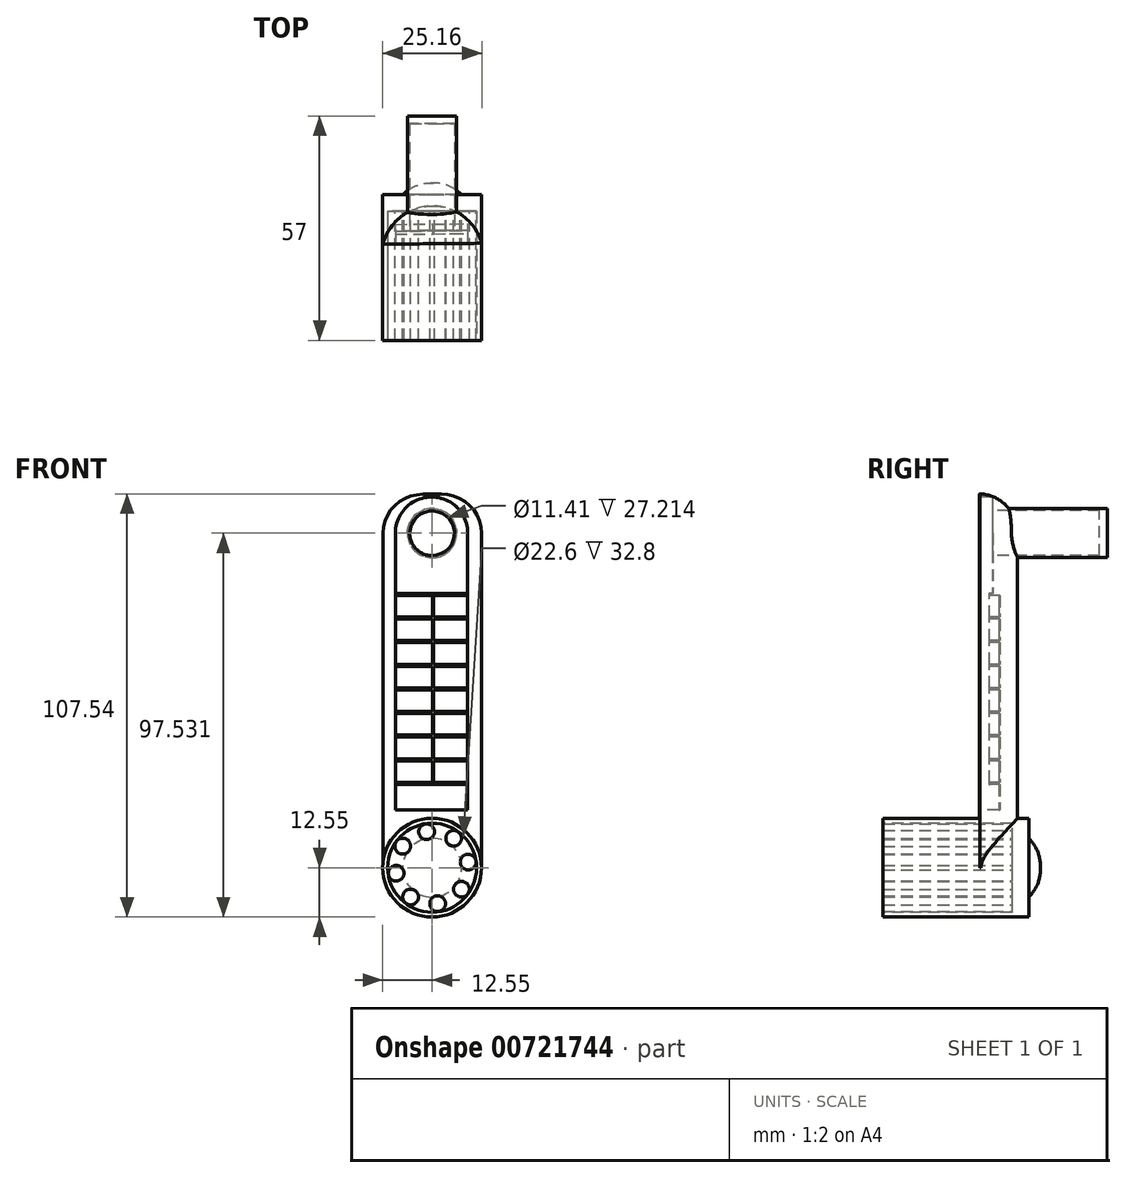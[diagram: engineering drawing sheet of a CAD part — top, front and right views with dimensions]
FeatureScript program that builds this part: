
annotation { "Feature Type Name" : "Feature", "Feature Type Description" : "" }
export const myFeature = defineFeature(function(context is Context, id is Id, definition is map)
    precondition{}
    {
        {
            var Q0;
            Q0=qCreatedBy(makeId("Front.planeOp"),FACE);
            var sketch = newSketch(context, id + "F0", { "sketchPlane" : qUnion([Q0])});
            skCircle(sketch, "E0", {"center": v(0, 0) * mm, "radius": 12.55 * mm});
            skSolve(sketch);
        }
        {
            var Q0;
            Q0=makeQuery(id+"F0.imprint","IMPRINT",FACE,{"disambiguationData":[TD([[makeQuery(id+"F0.imprint","IMPRINT",EDGE,{"derivedFrom":sQuery(id+"F0.wireOp",EDGE,"E0")}),1.0]])]});
            extrude(context, id + "F1", {"entities" : qUnion([Q0]), "depth" : 37 * mm, "offsetDistance" : 25 * mm});
        }
        {
            var Q0;
            Q0=qCreatedBy(makeId("Front.planeOp"),FACE);
            var sketch = newSketch(context, id + "F2", { "sketchPlane" : qUnion([Q0])});
            skCircle(sketch, "E1", {"center": v(0, 0) * mm, "radius": 7.5 * mm});
            skSolve(sketch);
        }
        {
            var Q0;
            Q0=qSketchRegion(id+"F2",true);
            extrude(context, id + "F3", {"entities" : qUnion([Q0]), "operationType" : NewBodyOperationType.ADD, "oppositeDirection" : true, "depth" : 3 * mm, "offsetDistance" : 25 * mm});
        }
        {
            var Q0;
            Q0=makeQuery(id+"F3.opExtrude","CAP_FACE",FACE,{"disambiguationData":[OSD([sQuery(id+"F2.wireOp",EDGE,"E1")])],"isStart":false});
            fillet(context, id + "F4", {"entities" : qUnion([Q0]), "radius" : 10 * mm, "tangentPropagation" : true, "allowEdgeOverflow" : false});
        }
        {
            var Q0;
            Q0=qCreatedBy(makeId("Top.planeOp"),FACE);
            var sketch = newSketch(context, id + "F5", { "sketchPlane" : qUnion([Q0])});
            skArc(sketch, "E2", {"start": v(12.6, -12.34) * mm, "mid": v(-0.03, -2.85) * mm, "end": v(-12.5, -12.58) * mm});
            skLineSegment(sketch, "E3", {"start": v(-12.5, -12.58) * mm, "end": v(12.6, -12.34) * mm});
            skSolve(sketch);
        }
        {
            var Q0;
            Q0=qSketchRegion(id+"F5",true);
            extrude(context, id + "F6", {"entities" : qUnion([Q0]), "operationType" : NewBodyOperationType.ADD, "depth" : 95 * mm, "offsetDistance" : 25 * mm});
        }
        {
            var Q0;
            Q0=makeQuery(id+"F6.opExtrude","CAP_EDGE",EDGE,{"disambiguationData":[OSD([sQuery(id+"F5.wireOp",EDGE,"E2")])],"isStart":false});
            fillet(context, id + "F7", {"entities" : qUnion([Q0]), "radius" : 10 * mm, "tangentPropagation" : true, "allowEdgeOverflow" : false});
        }
        {
            var Q0;
            Q0=qCreatedBy(makeId("Front.planeOp"),FACE);
            cPlane(context, id + "F8", {"entities" : qUnion([Q0]), "cplaneType" : CPlaneType.OFFSET, "offset" : 10 * mm, "width" : 150 * mm, "height" : 150 * mm});
        }
        {
            var Q0;
            Q0=qCreatedBy(id+"F8.planeOp",FACE);
            var sketch = newSketch(context, id + "F9", { "sketchPlane" : qUnion([Q0])});
            skCircle(sketch, "E4", {"center": v(-0.03, 85) * mm, "radius": 6.25 * mm});
            skSolve(sketch);
        }
        {
            var Q0;
            Q0=qSketchRegion(id+"F9",true);
            extrude(context, id + "F10", {"entities" : qUnion([Q0]), "operationType" : NewBodyOperationType.ADD, "oppositeDirection" : true, "depth" : 30 * mm, "offsetDistance" : 25 * mm});
        }
        {
            var Q0;
            Q0=makeQuery(id+"F6.opExtrude","SWEPT_FACE",FACE,{"disambiguationData":[OSD([sQuery(id+"F5.wireOp",EDGE,"E3")])]});
            var sketch = newSketch(context, id + "F11", { "sketchPlane" : qUnion([Q0])});
            skLineSegment(sketch, "E5.bottom", {"start": v(-9.45, 85) * mm, "end": v(8.93, 85) * mm});
            skLineSegment(sketch, "E5.top", {"start": v(-9.45, 14.71) * mm, "end": v(8.93, 14.71) * mm});
            skLineSegment(sketch, "E5.left", {"start": v(-9.45, 85) * mm, "end": v(-9.45, 14.71) * mm});
            skLineSegment(sketch, "E5.right", {"start": v(8.93, 85) * mm, "end": v(8.93, 14.71) * mm});
            skArc(sketch, "E6", {"start": v(8.93, 85) * mm, "mid": v(-0.26, 94.19) * mm, "end": v(-9.45, 85) * mm});
            skSolve(sketch);
        }
        {
            var Q0;
            Q0=makeQuery(id+"F11.imprint","IMPRINT",FACE,{"disambiguationData":[TD([[makeQuery(id+"F11.imprint","IMPRINT",EDGE,{"derivedFrom":sQuery(id+"F11.wireOp",EDGE,"E5.bottom")}),-1.0]])]});
            extrude(context, id + "F12", {"entities" : qUnion([Q0]), "operationType" : NewBodyOperationType.REMOVE, "oppositeDirection" : true, "depth" : 2 * mm, "offsetDistance" : 25 * mm});
        }
        {
            var Q0;
            Q0 = qSketchRegion(id + "F11", true);
            extrude(context, id + "F13", {"entities" : qUnion([Q0]), "operationType" : NewBodyOperationType.REMOVE, "oppositeDirection" : true, "depth" : 2.5 * mm, "offsetDistance" : 25 * mm});
        }
        {
            var Q0;
            Q0=makeQuery(id+"F13.boolean.opBoolean","COPY",FACE,{"derivedFrom":makeQuery(id+"F13.opExtrude","CAP_FACE",FACE,{"disambiguationData":[OSD([sQuery(id+"F11.wireOp",EDGE,"E5.top"),sQuery(id+"F11.wireOp",EDGE,"E5.left"),sQuery(id+"F11.wireOp",EDGE,"E5.right"),sQuery(id+"F11.wireOp",EDGE,"E6")])],"isStart":false})});
            var sketch = newSketch(context, id + "F14", { "sketchPlane" : qUnion([Q0])});
            skLineSegment(sketch, "E7", {"start": v(-9.45, 21.68) * mm, "end": v(8.93, 21.68) * mm});
            skLineSegment(sketch, "E8.0.1.0", {"start": v(-9.45, 27.68) * mm, "end": v(8.93, 27.68) * mm});
            skLineSegment(sketch, "E8.0.2.0", {"start": v(-9.45, 33.68) * mm, "end": v(8.93, 33.68) * mm});
            skLineSegment(sketch, "E8.0.3.0", {"start": v(-9.45, 39.68) * mm, "end": v(8.93, 39.68) * mm});
            skLineSegment(sketch, "E8.0.4.0", {"start": v(-9.45, 45.68) * mm, "end": v(8.93, 45.68) * mm});
            skLineSegment(sketch, "E8.0.5.0", {"start": v(-9.45, 51.68) * mm, "end": v(8.93, 51.68) * mm});
            skLineSegment(sketch, "E8.0.6.0", {"start": v(-9.45, 57.68) * mm, "end": v(8.93, 57.68) * mm});
            skLineSegment(sketch, "E8.0.7.0", {"start": v(-9.45, 63.68) * mm, "end": v(8.93, 63.68) * mm});
            skLineSegment(sketch, "E8.0.8.0", {"start": v(-9.45, 69.68) * mm, "end": v(8.93, 69.68) * mm});
            skLineSegment(sketch, "E8.direction1", {"start": v(-9.45, 21.68) * mm, "end": v(-9.45, 21.68) * mm});
            skLineSegment(sketch, "E8.direction2", {"start": v(-9.45, 21.68) * mm, "end": v(-9.45, 27.68) * mm, "construction": true});
            skLineSegment(sketch, "E9", {"start": v(0, 14.71) * mm, "end": v(0, 75.51) * mm});
            skLineSegment(sketch, "E10", {"start": v(-9.45, 21.16) * mm, "end": v(8.93, 21.16) * mm});
            skLineSegment(sketch, "E11.0.1.0", {"start": v(-9.45, 27.16) * mm, "end": v(8.93, 27.16) * mm});
            skLineSegment(sketch, "E11.0.2.0", {"start": v(-9.45, 33.16) * mm, "end": v(8.93, 33.16) * mm});
            skLineSegment(sketch, "E11.0.3.0", {"start": v(-9.45, 39.16) * mm, "end": v(8.93, 39.16) * mm});
            skLineSegment(sketch, "E11.0.4.0", {"start": v(-9.45, 45.16) * mm, "end": v(8.93, 45.16) * mm});
            skLineSegment(sketch, "E11.0.5.0", {"start": v(-9.45, 51.16) * mm, "end": v(8.93, 51.16) * mm});
            skLineSegment(sketch, "E11.0.6.0", {"start": v(-9.45, 57.16) * mm, "end": v(8.93, 57.16) * mm});
            skLineSegment(sketch, "E11.0.7.0", {"start": v(-9.45, 63.16) * mm, "end": v(8.93, 63.16) * mm});
            skLineSegment(sketch, "E11.0.8.0", {"start": v(-9.45, 69.16) * mm, "end": v(8.93, 69.16) * mm});
            skLineSegment(sketch, "E11.1.1.0", {"start": v(-9.45, 27.16) * mm, "end": v(8.93, 27.16) * mm});
            skLineSegment(sketch, "E11.1.2.0", {"start": v(-9.45, 33.16) * mm, "end": v(8.93, 33.16) * mm});
            skLineSegment(sketch, "E11.1.3.0", {"start": v(-9.45, 39.16) * mm, "end": v(8.93, 39.16) * mm});
            skLineSegment(sketch, "E11.1.4.0", {"start": v(-9.45, 45.16) * mm, "end": v(8.93, 45.16) * mm});
            skLineSegment(sketch, "E11.1.5.0", {"start": v(-9.45, 51.16) * mm, "end": v(8.93, 51.16) * mm});
            skLineSegment(sketch, "E11.1.6.0", {"start": v(-9.45, 57.16) * mm, "end": v(8.93, 57.16) * mm});
            skLineSegment(sketch, "E11.1.7.0", {"start": v(-9.45, 63.16) * mm, "end": v(8.93, 63.16) * mm});
            skLineSegment(sketch, "E11.1.8.0", {"start": v(-9.45, 69.16) * mm, "end": v(8.93, 69.16) * mm});
            skLineSegment(sketch, "E11.2.1.0", {"start": v(-9.45, 27.16) * mm, "end": v(8.93, 27.16) * mm});
            skLineSegment(sketch, "E11.2.2.0", {"start": v(-9.45, 33.16) * mm, "end": v(8.93, 33.16) * mm});
            skLineSegment(sketch, "E11.2.3.0", {"start": v(-9.45, 39.16) * mm, "end": v(8.93, 39.16) * mm});
            skLineSegment(sketch, "E11.2.4.0", {"start": v(-9.45, 45.16) * mm, "end": v(8.93, 45.16) * mm});
            skLineSegment(sketch, "E11.2.5.0", {"start": v(-9.45, 51.16) * mm, "end": v(8.93, 51.16) * mm});
            skLineSegment(sketch, "E11.2.6.0", {"start": v(-9.45, 57.16) * mm, "end": v(8.93, 57.16) * mm});
            skLineSegment(sketch, "E11.2.7.0", {"start": v(-9.45, 63.16) * mm, "end": v(8.93, 63.16) * mm});
            skLineSegment(sketch, "E11.2.8.0", {"start": v(-9.45, 69.16) * mm, "end": v(8.93, 69.16) * mm});
            skLineSegment(sketch, "E11.3.1.0", {"start": v(-9.45, 27.16) * mm, "end": v(8.93, 27.16) * mm});
            skLineSegment(sketch, "E11.3.2.0", {"start": v(-9.45, 33.16) * mm, "end": v(8.93, 33.16) * mm});
            skLineSegment(sketch, "E11.3.3.0", {"start": v(-9.45, 39.16) * mm, "end": v(8.93, 39.16) * mm});
            skLineSegment(sketch, "E11.3.4.0", {"start": v(-9.45, 45.16) * mm, "end": v(8.93, 45.16) * mm});
            skLineSegment(sketch, "E11.3.5.0", {"start": v(-9.45, 51.16) * mm, "end": v(8.93, 51.16) * mm});
            skLineSegment(sketch, "E11.3.6.0", {"start": v(-9.45, 57.16) * mm, "end": v(8.93, 57.16) * mm});
            skLineSegment(sketch, "E11.3.7.0", {"start": v(-9.45, 63.16) * mm, "end": v(8.93, 63.16) * mm});
            skLineSegment(sketch, "E11.3.8.0", {"start": v(-9.45, 69.16) * mm, "end": v(8.93, 69.16) * mm});
            skLineSegment(sketch, "E11.4.1.0", {"start": v(-9.45, 27.16) * mm, "end": v(8.93, 27.16) * mm});
            skLineSegment(sketch, "E11.4.2.0", {"start": v(-9.45, 33.16) * mm, "end": v(8.93, 33.16) * mm});
            skLineSegment(sketch, "E11.4.3.0", {"start": v(-9.45, 39.16) * mm, "end": v(8.93, 39.16) * mm});
            skLineSegment(sketch, "E11.4.4.0", {"start": v(-9.45, 45.16) * mm, "end": v(8.93, 45.16) * mm});
            skLineSegment(sketch, "E11.4.5.0", {"start": v(-9.45, 51.16) * mm, "end": v(8.93, 51.16) * mm});
            skLineSegment(sketch, "E11.4.6.0", {"start": v(-9.45, 57.16) * mm, "end": v(8.93, 57.16) * mm});
            skLineSegment(sketch, "E11.4.7.0", {"start": v(-9.45, 63.16) * mm, "end": v(8.93, 63.16) * mm});
            skLineSegment(sketch, "E11.4.8.0", {"start": v(-9.45, 69.16) * mm, "end": v(8.93, 69.16) * mm});
            skLineSegment(sketch, "E11.5.1.0", {"start": v(-9.45, 27.16) * mm, "end": v(8.93, 27.16) * mm});
            skLineSegment(sketch, "E11.5.2.0", {"start": v(-9.45, 33.16) * mm, "end": v(8.93, 33.16) * mm});
            skLineSegment(sketch, "E11.5.3.0", {"start": v(-9.45, 39.16) * mm, "end": v(8.93, 39.16) * mm});
            skLineSegment(sketch, "E11.5.4.0", {"start": v(-9.45, 45.16) * mm, "end": v(8.93, 45.16) * mm});
            skLineSegment(sketch, "E11.5.5.0", {"start": v(-9.45, 51.16) * mm, "end": v(8.93, 51.16) * mm});
            skLineSegment(sketch, "E11.5.6.0", {"start": v(-9.45, 57.16) * mm, "end": v(8.93, 57.16) * mm});
            skLineSegment(sketch, "E11.5.7.0", {"start": v(-9.45, 63.16) * mm, "end": v(8.93, 63.16) * mm});
            skLineSegment(sketch, "E11.5.8.0", {"start": v(-9.45, 69.16) * mm, "end": v(8.93, 69.16) * mm});
            skLineSegment(sketch, "E11.6.1.0", {"start": v(-9.45, 27.16) * mm, "end": v(8.93, 27.16) * mm});
            skLineSegment(sketch, "E11.6.2.0", {"start": v(-9.45, 33.16) * mm, "end": v(8.93, 33.16) * mm});
            skLineSegment(sketch, "E11.6.3.0", {"start": v(-9.45, 39.16) * mm, "end": v(8.93, 39.16) * mm});
            skLineSegment(sketch, "E11.6.4.0", {"start": v(-9.45, 45.16) * mm, "end": v(8.93, 45.16) * mm});
            skLineSegment(sketch, "E11.6.5.0", {"start": v(-9.45, 51.16) * mm, "end": v(8.93, 51.16) * mm});
            skLineSegment(sketch, "E11.6.6.0", {"start": v(-9.45, 57.16) * mm, "end": v(8.93, 57.16) * mm});
            skLineSegment(sketch, "E11.6.7.0", {"start": v(-9.45, 63.16) * mm, "end": v(8.93, 63.16) * mm});
            skLineSegment(sketch, "E11.6.8.0", {"start": v(-9.45, 69.16) * mm, "end": v(8.93, 69.16) * mm});
            skLineSegment(sketch, "E11.7.1.0", {"start": v(-9.45, 27.16) * mm, "end": v(8.93, 27.16) * mm});
            skLineSegment(sketch, "E11.7.2.0", {"start": v(-9.45, 33.16) * mm, "end": v(8.93, 33.16) * mm});
            skLineSegment(sketch, "E11.7.3.0", {"start": v(-9.45, 39.16) * mm, "end": v(8.93, 39.16) * mm});
            skLineSegment(sketch, "E11.7.4.0", {"start": v(-9.45, 45.16) * mm, "end": v(8.93, 45.16) * mm});
            skLineSegment(sketch, "E11.7.5.0", {"start": v(-9.45, 51.16) * mm, "end": v(8.93, 51.16) * mm});
            skLineSegment(sketch, "E11.7.6.0", {"start": v(-9.45, 57.16) * mm, "end": v(8.93, 57.16) * mm});
            skLineSegment(sketch, "E11.7.7.0", {"start": v(-9.45, 63.16) * mm, "end": v(8.93, 63.16) * mm});
            skLineSegment(sketch, "E11.7.8.0", {"start": v(-9.45, 69.16) * mm, "end": v(8.93, 69.16) * mm});
            skLineSegment(sketch, "E11.8.1.0", {"start": v(-9.45, 27.16) * mm, "end": v(8.93, 27.16) * mm});
            skLineSegment(sketch, "E11.8.2.0", {"start": v(-9.45, 33.16) * mm, "end": v(8.93, 33.16) * mm});
            skLineSegment(sketch, "E11.8.3.0", {"start": v(-9.45, 39.16) * mm, "end": v(8.93, 39.16) * mm});
            skLineSegment(sketch, "E11.8.4.0", {"start": v(-9.45, 45.16) * mm, "end": v(8.93, 45.16) * mm});
            skLineSegment(sketch, "E11.8.5.0", {"start": v(-9.45, 51.16) * mm, "end": v(8.93, 51.16) * mm});
            skLineSegment(sketch, "E11.8.6.0", {"start": v(-9.45, 57.16) * mm, "end": v(8.93, 57.16) * mm});
            skLineSegment(sketch, "E11.8.7.0", {"start": v(-9.45, 63.16) * mm, "end": v(8.93, 63.16) * mm});
            skLineSegment(sketch, "E11.8.8.0", {"start": v(-9.45, 69.16) * mm, "end": v(8.93, 69.16) * mm});
            skLineSegment(sketch, "E11.direction1", {"start": v(-9.45, 21.16) * mm, "end": v(-9.45, 21.16) * mm});
            skLineSegment(sketch, "E11.direction2", {"start": v(-9.45, 21.16) * mm, "end": v(-9.45, 27.16) * mm, "construction": true});
            skLineSegment(sketch, "E12", {"start": v(0.32, 14.71) * mm, "end": v(0.32, 75.5) * mm});
            skSolve(sketch);
        }
        {
            var Q0;
            {var subQ0=sQuery(id+"F14.wireOp",EDGE,"E9");var subQ1=makeQuery(id+"F13.boolean.opBoolean","COPY",EDGE,{"derivedFrom":makeQuery(id+"F13.opExtrude","CAP_EDGE",EDGE,{"disambiguationData":[OSD([sQuery(id+"F11.wireOp",EDGE,"E5.top")])],"isStart":false})});var subQ2=makeQuery(id+"F14.imprint","INTERSECT",VERTEX,{"derivedFrom":[subQ1,subQ0]});Q0=makeQuery(id+"F14.imprint","IMPRINT",FACE,{"disambiguationData":[TD([[makeQuery(id+"F14.imprint","IMPRINT",EDGE,{"disambiguationData":[TD([[subQ2,-1.0]])],"derivedFrom":subQ0}),1.0]])]});}
            var Q1;
            {var subQ0=sQuery(id+"F14.wireOp",EDGE,"E7");var subQ1=makeQuery(id+"F13.boolean.opBoolean","COPY",EDGE,{"derivedFrom":makeQuery(id+"F13.opExtrude","CAP_EDGE",EDGE,{"disambiguationData":[OSD([sQuery(id+"F11.wireOp",EDGE,"E5.left")])],"isStart":false})});var subQ2=makeQuery(id+"F14.imprint","INTERSECT",VERTEX,{"derivedFrom":[subQ1,subQ0]});Q1=makeQuery(id+"F14.imprint","IMPRINT",FACE,{"disambiguationData":[TD([[makeQuery(id+"F14.imprint","IMPRINT",EDGE,{"disambiguationData":[TD([[subQ2,-1.0]])],"derivedFrom":subQ0}),1.0]])]});}
            var Q2;
            {var subQ0=sQuery(id+"F14.wireOp",EDGE,"E8.0.1.0");var subQ1=makeQuery(id+"F13.boolean.opBoolean","COPY",EDGE,{"derivedFrom":makeQuery(id+"F13.opExtrude","CAP_EDGE",EDGE,{"disambiguationData":[OSD([sQuery(id+"F11.wireOp",EDGE,"E5.left")])],"isStart":false})});var subQ2=makeQuery(id+"F14.imprint","INTERSECT",VERTEX,{"derivedFrom":[subQ1,subQ0]});Q2=makeQuery(id+"F14.imprint","IMPRINT",FACE,{"disambiguationData":[TD([[makeQuery(id+"F14.imprint","IMPRINT",EDGE,{"disambiguationData":[TD([[subQ2,-1.0]])],"derivedFrom":subQ0}),1.0]])]});}
            var Q3;
            {var subQ0=sQuery(id+"F14.wireOp",EDGE,"E8.0.2.0");var subQ1=makeQuery(id+"F13.boolean.opBoolean","COPY",EDGE,{"derivedFrom":makeQuery(id+"F13.opExtrude","CAP_EDGE",EDGE,{"disambiguationData":[OSD([sQuery(id+"F11.wireOp",EDGE,"E5.left")])],"isStart":false})});var subQ2=makeQuery(id+"F14.imprint","INTERSECT",VERTEX,{"derivedFrom":[subQ1,subQ0]});Q3=makeQuery(id+"F14.imprint","IMPRINT",FACE,{"disambiguationData":[TD([[makeQuery(id+"F14.imprint","IMPRINT",EDGE,{"disambiguationData":[TD([[subQ2,-1.0]])],"derivedFrom":subQ0}),1.0]])]});}
            var Q4;
            {var subQ0=sQuery(id+"F14.wireOp",EDGE,"E8.0.3.0");var subQ1=makeQuery(id+"F13.boolean.opBoolean","COPY",EDGE,{"derivedFrom":makeQuery(id+"F13.opExtrude","CAP_EDGE",EDGE,{"disambiguationData":[OSD([sQuery(id+"F11.wireOp",EDGE,"E5.left")])],"isStart":false})});var subQ2=makeQuery(id+"F14.imprint","INTERSECT",VERTEX,{"derivedFrom":[subQ1,subQ0]});Q4=makeQuery(id+"F14.imprint","IMPRINT",FACE,{"disambiguationData":[TD([[makeQuery(id+"F14.imprint","IMPRINT",EDGE,{"disambiguationData":[TD([[subQ2,-1.0]])],"derivedFrom":subQ0}),1.0]])]});}
            var Q5;
            {var subQ0=sQuery(id+"F14.wireOp",EDGE,"E8.0.4.0");var subQ1=makeQuery(id+"F13.boolean.opBoolean","COPY",EDGE,{"derivedFrom":makeQuery(id+"F13.opExtrude","CAP_EDGE",EDGE,{"disambiguationData":[OSD([sQuery(id+"F11.wireOp",EDGE,"E5.left")])],"isStart":false})});var subQ2=makeQuery(id+"F14.imprint","INTERSECT",VERTEX,{"derivedFrom":[subQ1,subQ0]});Q5=makeQuery(id+"F14.imprint","IMPRINT",FACE,{"disambiguationData":[TD([[makeQuery(id+"F14.imprint","IMPRINT",EDGE,{"disambiguationData":[TD([[subQ2,-1.0]])],"derivedFrom":subQ0}),1.0]])]});}
            var Q6;
            {var subQ0=sQuery(id+"F14.wireOp",EDGE,"E8.0.5.0");var subQ1=makeQuery(id+"F13.boolean.opBoolean","COPY",EDGE,{"derivedFrom":makeQuery(id+"F13.opExtrude","CAP_EDGE",EDGE,{"disambiguationData":[OSD([sQuery(id+"F11.wireOp",EDGE,"E5.left")])],"isStart":false})});var subQ2=makeQuery(id+"F14.imprint","INTERSECT",VERTEX,{"derivedFrom":[subQ1,subQ0]});Q6=makeQuery(id+"F14.imprint","IMPRINT",FACE,{"disambiguationData":[TD([[makeQuery(id+"F14.imprint","IMPRINT",EDGE,{"disambiguationData":[TD([[subQ2,-1.0]])],"derivedFrom":subQ0}),1.0]])]});}
            var Q7;
            {var subQ0=sQuery(id+"F14.wireOp",EDGE,"E8.0.6.0");var subQ1=makeQuery(id+"F13.boolean.opBoolean","COPY",EDGE,{"derivedFrom":makeQuery(id+"F13.opExtrude","CAP_EDGE",EDGE,{"disambiguationData":[OSD([sQuery(id+"F11.wireOp",EDGE,"E5.left")])],"isStart":false})});var subQ2=makeQuery(id+"F14.imprint","INTERSECT",VERTEX,{"derivedFrom":[subQ1,subQ0]});Q7=makeQuery(id+"F14.imprint","IMPRINT",FACE,{"disambiguationData":[TD([[makeQuery(id+"F14.imprint","IMPRINT",EDGE,{"disambiguationData":[TD([[subQ2,-1.0]])],"derivedFrom":subQ0}),1.0]])]});}
            var Q8;
            {var subQ0=sQuery(id+"F14.wireOp",EDGE,"E8.0.7.0");var subQ1=makeQuery(id+"F13.boolean.opBoolean","COPY",EDGE,{"derivedFrom":makeQuery(id+"F13.opExtrude","CAP_EDGE",EDGE,{"disambiguationData":[OSD([sQuery(id+"F11.wireOp",EDGE,"E5.left")])],"isStart":false})});var subQ2=makeQuery(id+"F14.imprint","INTERSECT",VERTEX,{"derivedFrom":[subQ1,subQ0]});Q8=makeQuery(id+"F14.imprint","IMPRINT",FACE,{"disambiguationData":[TD([[makeQuery(id+"F14.imprint","IMPRINT",EDGE,{"disambiguationData":[TD([[subQ2,-1.0]])],"derivedFrom":subQ0}),1.0]])]});}
            var Q9;
            {var subQ0=sQuery(id+"F14.wireOp",EDGE,"E8.0.7.0");var subQ1=makeQuery(id+"F13.boolean.opBoolean","COPY",EDGE,{"derivedFrom":makeQuery(id+"F13.opExtrude","CAP_EDGE",EDGE,{"disambiguationData":[OSD([sQuery(id+"F11.wireOp",EDGE,"E5.right")])],"isStart":false})});var subQ2=makeQuery(id+"F14.imprint","INTERSECT",VERTEX,{"derivedFrom":[subQ1,subQ0]});Q9=makeQuery(id+"F14.imprint","IMPRINT",FACE,{"disambiguationData":[TD([[makeQuery(id+"F14.imprint","IMPRINT",EDGE,{"disambiguationData":[TD([[subQ2,1.0]])],"derivedFrom":subQ0}),1.0]])]});}
            var Q10;
            {var subQ0=sQuery(id+"F14.wireOp",EDGE,"E8.0.6.0");var subQ1=makeQuery(id+"F13.boolean.opBoolean","COPY",EDGE,{"derivedFrom":makeQuery(id+"F13.opExtrude","CAP_EDGE",EDGE,{"disambiguationData":[OSD([sQuery(id+"F11.wireOp",EDGE,"E5.right")])],"isStart":false})});var subQ2=makeQuery(id+"F14.imprint","INTERSECT",VERTEX,{"derivedFrom":[subQ1,subQ0]});Q10=makeQuery(id+"F14.imprint","IMPRINT",FACE,{"disambiguationData":[TD([[makeQuery(id+"F14.imprint","IMPRINT",EDGE,{"disambiguationData":[TD([[subQ2,1.0]])],"derivedFrom":subQ0}),1.0]])]});}
            var Q11;
            {var subQ0=sQuery(id+"F14.wireOp",EDGE,"E8.0.5.0");var subQ1=makeQuery(id+"F13.boolean.opBoolean","COPY",EDGE,{"derivedFrom":makeQuery(id+"F13.opExtrude","CAP_EDGE",EDGE,{"disambiguationData":[OSD([sQuery(id+"F11.wireOp",EDGE,"E5.right")])],"isStart":false})});var subQ2=makeQuery(id+"F14.imprint","INTERSECT",VERTEX,{"derivedFrom":[subQ1,subQ0]});Q11=makeQuery(id+"F14.imprint","IMPRINT",FACE,{"disambiguationData":[TD([[makeQuery(id+"F14.imprint","IMPRINT",EDGE,{"disambiguationData":[TD([[subQ2,1.0]])],"derivedFrom":subQ0}),1.0]])]});}
            var Q12;
            {var subQ0=sQuery(id+"F14.wireOp",EDGE,"E8.0.4.0");var subQ1=makeQuery(id+"F13.boolean.opBoolean","COPY",EDGE,{"derivedFrom":makeQuery(id+"F13.opExtrude","CAP_EDGE",EDGE,{"disambiguationData":[OSD([sQuery(id+"F11.wireOp",EDGE,"E5.right")])],"isStart":false})});var subQ2=makeQuery(id+"F14.imprint","INTERSECT",VERTEX,{"derivedFrom":[subQ1,subQ0]});Q12=makeQuery(id+"F14.imprint","IMPRINT",FACE,{"disambiguationData":[TD([[makeQuery(id+"F14.imprint","IMPRINT",EDGE,{"disambiguationData":[TD([[subQ2,1.0]])],"derivedFrom":subQ0}),1.0]])]});}
            var Q13;
            {var subQ0=sQuery(id+"F14.wireOp",EDGE,"E8.0.3.0");var subQ1=makeQuery(id+"F13.boolean.opBoolean","COPY",EDGE,{"derivedFrom":makeQuery(id+"F13.opExtrude","CAP_EDGE",EDGE,{"disambiguationData":[OSD([sQuery(id+"F11.wireOp",EDGE,"E5.right")])],"isStart":false})});var subQ2=makeQuery(id+"F14.imprint","INTERSECT",VERTEX,{"derivedFrom":[subQ1,subQ0]});Q13=makeQuery(id+"F14.imprint","IMPRINT",FACE,{"disambiguationData":[TD([[makeQuery(id+"F14.imprint","IMPRINT",EDGE,{"disambiguationData":[TD([[subQ2,1.0]])],"derivedFrom":subQ0}),1.0]])]});}
            var Q14;
            {var subQ0=sQuery(id+"F14.wireOp",EDGE,"E8.0.2.0");var subQ1=makeQuery(id+"F13.boolean.opBoolean","COPY",EDGE,{"derivedFrom":makeQuery(id+"F13.opExtrude","CAP_EDGE",EDGE,{"disambiguationData":[OSD([sQuery(id+"F11.wireOp",EDGE,"E5.right")])],"isStart":false})});var subQ2=makeQuery(id+"F14.imprint","INTERSECT",VERTEX,{"derivedFrom":[subQ1,subQ0]});Q14=makeQuery(id+"F14.imprint","IMPRINT",FACE,{"disambiguationData":[TD([[makeQuery(id+"F14.imprint","IMPRINT",EDGE,{"disambiguationData":[TD([[subQ2,1.0]])],"derivedFrom":subQ0}),1.0]])]});}
            var Q15;
            {var subQ0=sQuery(id+"F14.wireOp",EDGE,"E8.0.1.0");var subQ1=makeQuery(id+"F13.boolean.opBoolean","COPY",EDGE,{"derivedFrom":makeQuery(id+"F13.opExtrude","CAP_EDGE",EDGE,{"disambiguationData":[OSD([sQuery(id+"F11.wireOp",EDGE,"E5.right")])],"isStart":false})});var subQ2=makeQuery(id+"F14.imprint","INTERSECT",VERTEX,{"derivedFrom":[subQ1,subQ0]});Q15=makeQuery(id+"F14.imprint","IMPRINT",FACE,{"disambiguationData":[TD([[makeQuery(id+"F14.imprint","IMPRINT",EDGE,{"disambiguationData":[TD([[subQ2,1.0]])],"derivedFrom":subQ0}),1.0]])]});}
            var Q16;
            {var subQ0=sQuery(id+"F14.wireOp",EDGE,"E7");var subQ1=makeQuery(id+"F13.boolean.opBoolean","COPY",EDGE,{"derivedFrom":makeQuery(id+"F13.opExtrude","CAP_EDGE",EDGE,{"disambiguationData":[OSD([sQuery(id+"F11.wireOp",EDGE,"E5.right")])],"isStart":false})});var subQ2=makeQuery(id+"F14.imprint","INTERSECT",VERTEX,{"derivedFrom":[subQ1,subQ0]});Q16=makeQuery(id+"F14.imprint","IMPRINT",FACE,{"disambiguationData":[TD([[makeQuery(id+"F14.imprint","IMPRINT",EDGE,{"disambiguationData":[TD([[subQ2,1.0]])],"derivedFrom":subQ0}),1.0]])]});}
            var Q17;
            {var subQ0=sQuery(id+"F14.wireOp",EDGE,"E9");var subQ1=makeQuery(id+"F13.boolean.opBoolean","COPY",EDGE,{"derivedFrom":makeQuery(id+"F13.opExtrude","CAP_EDGE",EDGE,{"disambiguationData":[OSD([sQuery(id+"F11.wireOp",EDGE,"E5.top")])],"isStart":false})});var subQ2=makeQuery(id+"F14.imprint","INTERSECT",VERTEX,{"derivedFrom":[subQ1,subQ0]});Q17=makeQuery(id+"F14.imprint","IMPRINT",FACE,{"disambiguationData":[TD([[makeQuery(id+"F14.imprint","IMPRINT",EDGE,{"disambiguationData":[TD([[subQ2,-1.0]])],"derivedFrom":subQ0}),-1.0]])]});}
            var Q18;
            {var subQ0=sQuery(id+"F14.wireOp",EDGE,"E10");var subQ1=makeQuery(id+"F13.boolean.opBoolean","COPY",EDGE,{"derivedFrom":makeQuery(id+"F13.opExtrude","CAP_EDGE",EDGE,{"disambiguationData":[OSD([sQuery(id+"F11.wireOp",EDGE,"E5.right")])],"isStart":false})});var subQ2=makeQuery(id+"F14.imprint","INTERSECT",VERTEX,{"derivedFrom":[subQ1,subQ0]});Q18=makeQuery(id+"F14.imprint","IMPRINT",FACE,{"disambiguationData":[TD([[makeQuery(id+"F14.imprint","IMPRINT",EDGE,{"disambiguationData":[TD([[subQ2,1.0]])],"derivedFrom":subQ0}),-1.0]])]});}
            extrude(context, id + "F15", {"entities" : qUnion([Q0, Q1, Q2, Q3, Q4, Q5, Q6, Q7, Q8, Q9, Q10, Q11, Q12, Q13, Q14, Q15, Q16, Q17, Q18]), "operationType" : NewBodyOperationType.REMOVE, "oppositeDirection" : true, "depth" : 2.5 * mm, "offsetDistance" : 25 * mm});
        }
        {
            var Q0;
            {var subQ4=makeQuery(id+"F13.boolean.opBoolean","COPY",EDGE,{"derivedFrom":makeQuery(id+"F13.opExtrude","CAP_EDGE",EDGE,{"disambiguationData":[OSD([sQuery(id+"F11.wireOp",EDGE,"E6")])],"isStart":false})});Q0=makeQuery(id+"F14.imprint","IMPRINT",FACE,{"disambiguationData":[TD([[makeQuery(id+"F14.imprint","IMPRINT",EDGE,{"derivedFrom":subQ4}),1.0]])]});}
            extrude(context, id + "F16", {"entities" : qUnion([Q0]), "operationType" : NewBodyOperationType.REMOVE, "oppositeDirection" : true, "depth" : 0.8 * mm, "offsetDistance" : 25 * mm});
        }
        {
            var Q0;
            Q0=makeQuery(id+"F9.imprint","IMPRINT",FACE,{"disambiguationData":[TD([[makeQuery(id+"F9.imprint","IMPRINT",EDGE,{"derivedFrom":sQuery(id+"F9.wireOp",EDGE,"E4")}),1.0]])]});
            var sketch = newSketch(context, id + "F17", { "sketchPlane" : qUnion([Q0])});
            skCircle(sketch, "E13", {"center": v(0, 84.98) * mm, "radius": 5.7 * mm});
            skSolve(sketch);
        }
        {
            var Q0;
            Q0=makeQuery(id+"F17.imprint","IMPRINT",FACE,{"disambiguationData":[TD([[makeQuery(id+"F17.imprint","IMPRINT",EDGE,{"derivedFrom":sQuery(id+"F17.wireOp",EDGE,"E13")}),1.0]])]});
            extrude(context, id + "F18", {"entities" : qUnion([Q0]), "operationType" : NewBodyOperationType.REMOVE, "oppositeDirection" : true, "depth" : 28 * mm, "offsetDistance" : 25 * mm});
        }
        {
            var Q0;
            Q0=makeQuery(id+"F1.opExtrude","CAP_FACE",FACE,{"disambiguationData":[OSD([sQuery(id+"F0.wireOp",EDGE,"E0")])],"isStart":false});
            var sketch = newSketch(context, id + "F19", { "sketchPlane" : qUnion([Q0])});
            skCircle(sketch, "E14", {"center": v(0, 0) * mm, "radius": 11.3 * mm});
            skSolve(sketch);
        }
        {
            var Q0;
            Q0=makeQuery(id+"F19.imprint","IMPRINT",FACE,{"disambiguationData":[TD([[makeQuery(id+"F19.imprint","IMPRINT",EDGE,{"derivedFrom":sQuery(id+"F19.wireOp",EDGE,"E14")}),1.0]])]});
            extrude(context, id + "F20", {"entities" : qUnion([Q0]), "operationType" : NewBodyOperationType.REMOVE, "oppositeDirection" : true, "depth" : 32.8 * mm, "offsetDistance" : 25 * mm});
        }
        {
            var Q0;
            Q0=makeQuery(id+"F20.boolean.opBoolean","COPY",FACE,{"derivedFrom":makeQuery(id+"F20.opExtrude","CAP_FACE",FACE,{"disambiguationData":[OSD([sQuery(id+"F19.wireOp",EDGE,"E14")])],"isStart":false})});
            var sketch = newSketch(context, id + "F21", { "sketchPlane" : qUnion([Q0])});
            skCircle(sketch, "E15", {"center": v(-7.46, 5.47) * mm, "radius": 2 * mm});
            skCircle(sketch, "E16.1.0", {"center": v(-9.14, -1.4) * mm, "radius": 2 * mm});
            skCircle(sketch, "E16.2.0", {"center": v(-5.47, -7.46) * mm, "radius": 2 * mm});
            skCircle(sketch, "E16.3.0", {"center": v(1.4, -9.14) * mm, "radius": 2 * mm});
            skCircle(sketch, "E16.4.0", {"center": v(7.46, -5.47) * mm, "radius": 2 * mm});
            skCircle(sketch, "E16.5.0", {"center": v(9.14, 1.4) * mm, "radius": 2 * mm});
            skCircle(sketch, "E16.6.0", {"center": v(5.47, 7.46) * mm, "radius": 2 * mm});
            skCircle(sketch, "E16.7.0", {"center": v(-1.4, 9.14) * mm, "radius": 2 * mm});
            skPoint(sketch, "E16.center", {"position": v(0, 0) * mm});
            skSolve(sketch);
        }
        {
            var Q0;
            Q0 = qSketchRegion(id + "F21", true);
            extrude(context, id + "F22", {"entities" : qUnion([Q0]), "operationType" : NewBodyOperationType.ADD, "depth" : 32.8 * mm, "offsetDistance" : 25 * mm});
        }
    });
